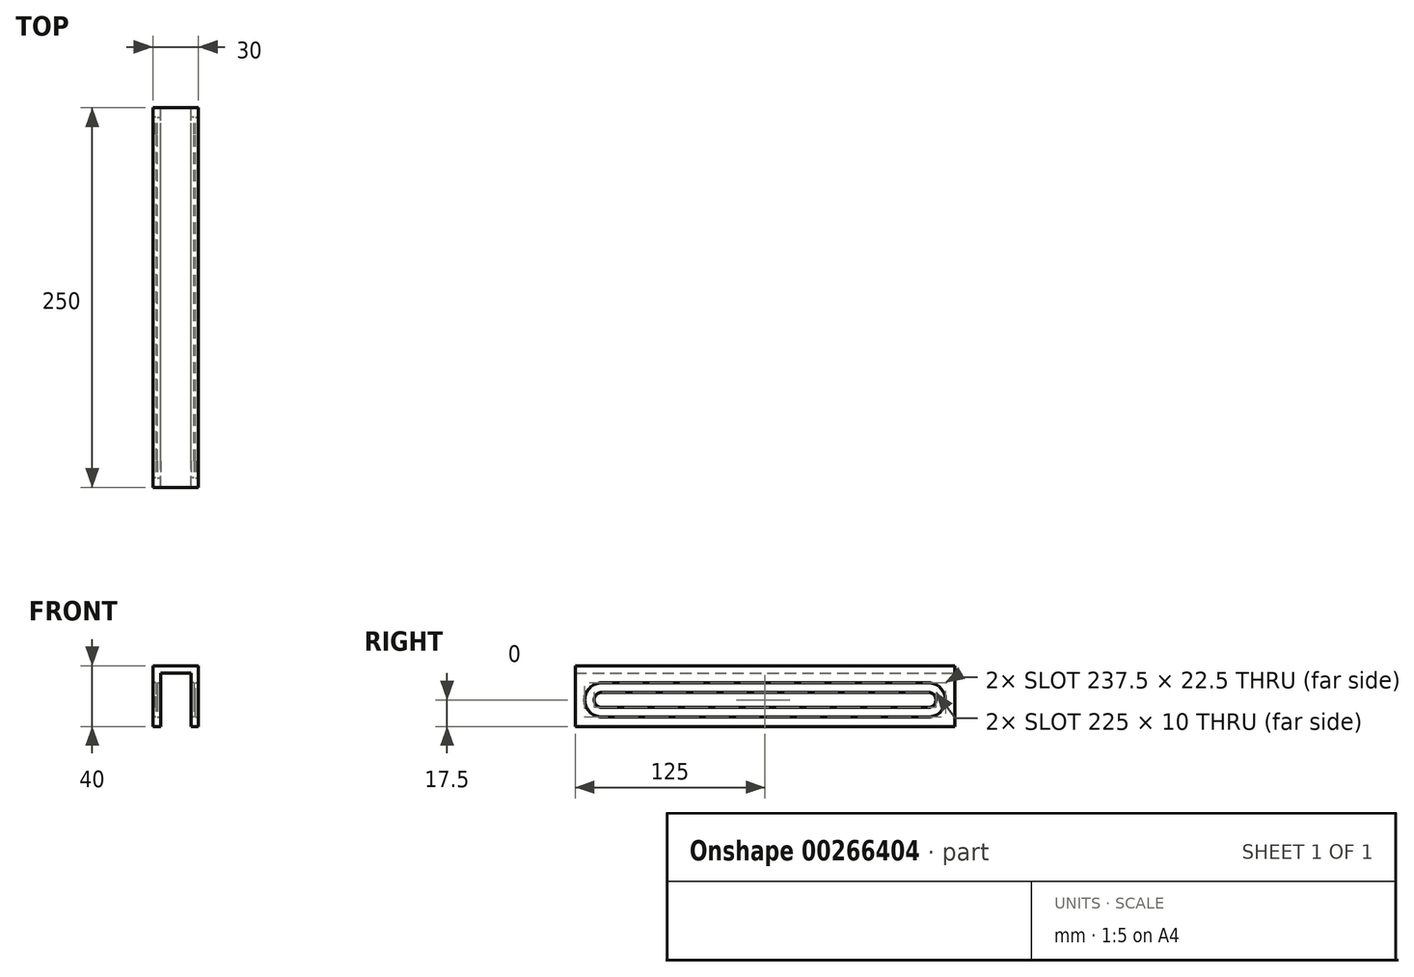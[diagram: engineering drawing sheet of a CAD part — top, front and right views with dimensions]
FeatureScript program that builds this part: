
annotation { "Feature Type Name" : "Feature", "Feature Type Description" : "" }
export const myFeature = defineFeature(function(context is Context, id is Id, definition is map)
    precondition{}
    {
        {
            var Q0;
            Q0=qCreatedBy(makeId("Front.planeOp"),FACE);
            var sketch = newSketch(context, id + "F0", { "sketchPlane" : qUnion([Q0])});
            skLineSegment(sketch, "E0.top", {"start": v(15, 20) * mm, "end": v(-15, 20) * mm});
            skLineSegment(sketch, "E0.left", {"start": v(15, -20) * mm, "end": v(15, 20) * mm});
            skLineSegment(sketch, "E0.right", {"start": v(-15, -20) * mm, "end": v(-15, 20) * mm});
            skPoint(sketch, "E0.middle", {"position": v(0, 0) * mm});
            skLineSegment(sketch, "E1", {"start": v(-15, -20) * mm, "end": v(-10, -20) * mm});
            skLineSegment(sketch, "E2", {"start": v(-10, -20) * mm, "end": v(-10, 15) * mm});
            skLineSegment(sketch, "E3", {"start": v(-10, 15) * mm, "end": v(10, 15) * mm});
            skLineSegment(sketch, "E4", {"start": v(10, 15) * mm, "end": v(10, -20) * mm});
            skLineSegment(sketch, "E5", {"start": v(10, -20) * mm, "end": v(15, -20) * mm});
            skSolve(sketch);
        }
        {
            var Q0;
            Q0=makeQuery(id+"F0.imprint","IMPRINT",FACE,{"disambiguationData":[TD([[makeQuery(id+"F0.imprint","IMPRINT",EDGE,{"derivedFrom":sQuery(id+"F0.wireOp",EDGE,"E0.top")}),1.0]])]});
            extrude(context, id + "F1", {"entities" : qUnion([Q0]), "depth" : 125 * mm, "hasSecondDirection" : true, "secondDirectionOppositeDirection" : true, "secondDirectionDepth" : 125 * mm});
        }
        {
            var Q0;
            Q0=makeQuery(id+"F1.opExtrude","SWEPT_FACE",FACE,{"disambiguationData":[OSD([sQuery(id+"F0.wireOp",EDGE,"E4")])]});
            var sketch = newSketch(context, id + "F2", { "sketchPlane" : qUnion([Q0])});
            skLineSegment(sketch, "E6", {"start": v(107.5, -13.75) * mm, "end": v(-107.5, -13.75) * mm});
            skLineSegment(sketch, "E7", {"start": v(107.5, 8.75) * mm, "end": v(-107.5, 8.75) * mm});
            skLineSegment(sketch, "E8", {"start": v(107.5, -7.5) * mm, "end": v(-107.5, -7.5) * mm});
            skLineSegment(sketch, "E9", {"start": v(107.5, 2.5) * mm, "end": v(-107.5, 2.5) * mm});
            skArc(sketch, "E10", {"start": v(-107.5, 2.5) * mm, "mid": v(-112.5, -2.5) * mm, "end": v(-107.5, -7.5) * mm});
            skArc(sketch, "E11", {"start": v(-107.5, 8.75) * mm, "mid": v(-118.75, -2.5) * mm, "end": v(-107.5, -13.75) * mm});
            skArc(sketch, "E12", {"start": v(107.5, -7.5) * mm, "mid": v(112.5, -2.5) * mm, "end": v(107.5, 2.5) * mm});
            skArc(sketch, "E13", {"start": v(107.5, -13.75) * mm, "mid": v(118.75, -2.5) * mm, "end": v(107.5, 8.75) * mm});
            skSolve(sketch);
        }
        {
            var Q0;
            Q0=makeQuery(id+"F1.opExtrude","SWEPT_FACE",FACE,{"disambiguationData":[OSD([sQuery(id+"F0.wireOp",EDGE,"E0.left")])]});
            var sketch = newSketch(context, id + "F3", { "sketchPlane" : qUnion([Q0])});
            skLineSegment(sketch, "E14", {"start": v(-107.5, -13.75) * mm, "end": v(107.5, -13.75) * mm});
            skLineSegment(sketch, "E15", {"start": v(-107.5, 8.75) * mm, "end": v(107.5, 8.75) * mm});
            skLineSegment(sketch, "E16", {"start": v(-107.5, 2.5) * mm, "end": v(107.5, 2.5) * mm});
            skLineSegment(sketch, "E17", {"start": v(-107.5, -7.5) * mm, "end": v(107.5, -7.5) * mm});
            skArc(sketch, "E18", {"start": v(-107.5, 2.5) * mm, "mid": v(-112.5, -2.5) * mm, "end": v(-107.5, -7.5) * mm});
            skArc(sketch, "E19", {"start": v(107.5, -7.5) * mm, "mid": v(112.5, -2.5) * mm, "end": v(107.5, 2.5) * mm});
            skArc(sketch, "E20", {"start": v(107.5, -13.75) * mm, "mid": v(118.75, -2.5) * mm, "end": v(107.5, 8.75) * mm});
            skArc(sketch, "E21", {"start": v(-107.5, 8.75) * mm, "mid": v(-118.75, -2.5) * mm, "end": v(-107.5, -13.75) * mm});
            skSolve(sketch);
        }
        {
            var Q0;
            Q0=makeQuery(id+"F1.opExtrude","SWEPT_FACE",FACE,{"disambiguationData":[OSD([sQuery(id+"F0.wireOp",EDGE,"E2")])]});
            var sketch = newSketch(context, id + "F4", { "sketchPlane" : qUnion([Q0])});
            skLineSegment(sketch, "E22", {"start": v(-107.5, 8.75) * mm, "end": v(107.5, 8.75) * mm});
            skLineSegment(sketch, "E23", {"start": v(-107.5, -13.75) * mm, "end": v(107.5, -13.75) * mm});
            skLineSegment(sketch, "E24", {"start": v(-107.5, 2.5) * mm, "end": v(107.5, 2.5) * mm});
            skLineSegment(sketch, "E25", {"start": v(-107.5, -7.5) * mm, "end": v(107.5, -7.5) * mm});
            skPoint(sketch, "E26.start.orphan", {"position": v(125, -2.5) * mm});
            skPoint(sketch, "E27.start.orphan", {"position": v(-125, -2.5) * mm});
            skArc(sketch, "E28", {"start": v(-107.5, 2.5) * mm, "mid": v(-112.5, -2.5) * mm, "end": v(-107.5, -7.5) * mm});
            skArc(sketch, "E29", {"start": v(-107.5, 8.75) * mm, "mid": v(-118.75, -2.5) * mm, "end": v(-107.5, -13.75) * mm});
            skArc(sketch, "E30", {"start": v(107.5, -7.5) * mm, "mid": v(112.5, -2.5) * mm, "end": v(107.5, 2.5) * mm});
            skArc(sketch, "E31", {"start": v(107.5, -13.75) * mm, "mid": v(118.75, -2.5) * mm, "end": v(107.5, 8.75) * mm});
            skSolve(sketch);
        }
        {
            var Q0;
            Q0=makeQuery(id+"F1.opExtrude","SWEPT_FACE",FACE,{"disambiguationData":[OSD([sQuery(id+"F0.wireOp",EDGE,"E0.right")])]});
            var sketch = newSketch(context, id + "F5", { "sketchPlane" : qUnion([Q0])});
            skLineSegment(sketch, "E32", {"start": v(-107.5, 8.75) * mm, "end": v(107.5, 8.75) * mm});
            skLineSegment(sketch, "E33", {"start": v(-107.5, -13.75) * mm, "end": v(107.5, -13.75) * mm});
            skLineSegment(sketch, "E34", {"start": v(-107.5, 2.5) * mm, "end": v(107.5, 2.5) * mm});
            skLineSegment(sketch, "E35", {"start": v(-107.5, -7.5) * mm, "end": v(107.5, -7.5) * mm});
            skArc(sketch, "E36", {"start": v(-107.5, 8.75) * mm, "mid": v(-118.75, -2.5) * mm, "end": v(-107.5, -13.75) * mm});
            skArc(sketch, "E37", {"start": v(-107.5, 2.5) * mm, "mid": v(-112.5, -2.5) * mm, "end": v(-107.5, -7.5) * mm});
            skArc(sketch, "E38", {"start": v(107.5, -7.5) * mm, "mid": v(112.5, -2.5) * mm, "end": v(107.5, 2.5) * mm});
            skArc(sketch, "E39", {"start": v(107.5, -13.75) * mm, "mid": v(118.75, -2.5) * mm, "end": v(107.5, 8.75) * mm});
            skSolve(sketch);
        }
        {
            var Q0;
            Q0=makeQuery(id+"F4.imprint","IMPRINT",FACE,{"disambiguationData":[TD([[makeQuery(id+"F4.imprint","IMPRINT",EDGE,{"derivedFrom":sQuery(id+"F4.wireOp",EDGE,"E24")}),-1.0]])]});
            extrude(context, id + "F6", {"entities" : qUnion([Q0]), "operationType" : NewBodyOperationType.REMOVE, "endBound" : BoundingType.THROUGH_ALL, "oppositeDirection" : true, "depth" : 25 * mm});
        }
        {
            var Q0;
            Q0=makeQuery(id+"F2.imprint","IMPRINT",FACE,{"disambiguationData":[TD([[makeQuery(id+"F2.imprint","IMPRINT",EDGE,{"derivedFrom":sQuery(id+"F2.wireOp",EDGE,"E8")}),-1.0]])]});
            extrude(context, id + "F7", {"entities" : qUnion([Q0]), "operationType" : NewBodyOperationType.REMOVE, "endBound" : BoundingType.THROUGH_ALL, "oppositeDirection" : true, "depth" : 25 * mm});
        }
        {
            var Q0;
            Q0=makeQuery(id+"F5.imprint","IMPRINT",FACE,{"disambiguationData":[TD([[makeQuery(id+"F5.imprint","IMPRINT",EDGE,{"derivedFrom":sQuery(id+"F5.wireOp",EDGE,"E32")}),-1.0]])]});
            extrude(context, id + "F8", {"entities" : qUnion([Q0]), "operationType" : NewBodyOperationType.REMOVE, "oppositeDirection" : true, "depth" : 2 * mm});
        }
        {
            var Q0;
            Q0=makeQuery(id+"F4.imprint","IMPRINT",FACE,{"disambiguationData":[TD([[makeQuery(id+"F4.imprint","IMPRINT",EDGE,{"derivedFrom":sQuery(id+"F4.wireOp",EDGE,"E22")}),-1.0]])]});
            extrude(context, id + "F9", {"entities" : qUnion([Q0]), "operationType" : NewBodyOperationType.REMOVE, "oppositeDirection" : true, "depth" : 2 * mm});
        }
        {
            var Q0;
            Q0=makeQuery(id+"F3.imprint","IMPRINT",FACE,{"disambiguationData":[TD([[makeQuery(id+"F3.imprint","IMPRINT",EDGE,{"derivedFrom":sQuery(id+"F3.wireOp",EDGE,"E14")}),1.0]])]});
            extrude(context, id + "F10", {"entities" : qUnion([Q0]), "operationType" : NewBodyOperationType.REMOVE, "oppositeDirection" : true, "depth" : 2 * mm});
        }
        {
            var Q0;
            Q0=makeQuery(id+"F2.imprint","IMPRINT",FACE,{"disambiguationData":[TD([[makeQuery(id+"F2.imprint","IMPRINT",EDGE,{"derivedFrom":sQuery(id+"F2.wireOp",EDGE,"E6")}),-1.0]])]});
            extrude(context, id + "F11", {"entities" : qUnion([Q0]), "operationType" : NewBodyOperationType.REMOVE, "oppositeDirection" : true, "depth" : 2 * mm});
        }
    });
